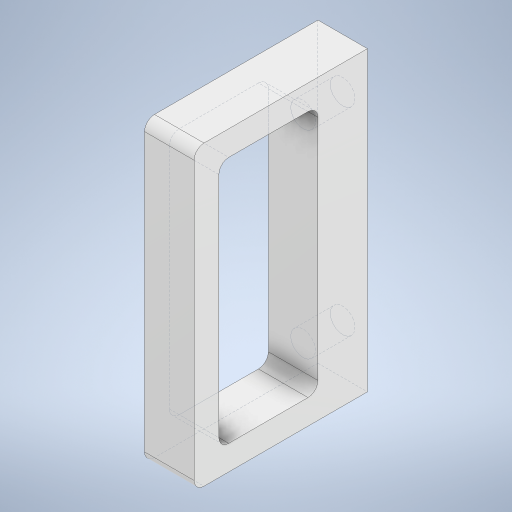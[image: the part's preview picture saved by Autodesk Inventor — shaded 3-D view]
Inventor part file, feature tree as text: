
AUTODESK INVENTOR PART (.ipt)
format: ipt  version: 2024.3 (Build 283343000, 343)  size: 266,240 bytes
history: native  units: mm
features: sketch x4, extrude x3, other x1, hole x1, fillet x1, projected_geometry x1
ambient origin geometry x8: Origin, YZ Plane, XZ Plane, XY Plane, X Axis, Y Axis, Z Axis, Center Point
bodies: Body1 (feature_tree)
feature tree (11):
  other  "ソリッド1"
  extrude  "押し出し1"  Depth=10.0mm
  extrude  "押し出し2"  Depth=60.0mm
  extrude  "押し出し3"  Depth=5.0mm TaperAngle=0.0deg
  hole  "穴2"  [1 undecoded]
  fillet  "フィレット1"  Radius=40.0mm
  sketch  "スケッチ1"
  sketch  "スケッチ3"
  projected_geometry  "投影ループ1"
  sketch  "スケッチ4"
  sketch  "スケッチ5"
note: 1 required parameter value undecoded (feature->parameter linkage not recoverable at this tier; creation-order binding heuristic only, values carry confidence <= 0.55)
